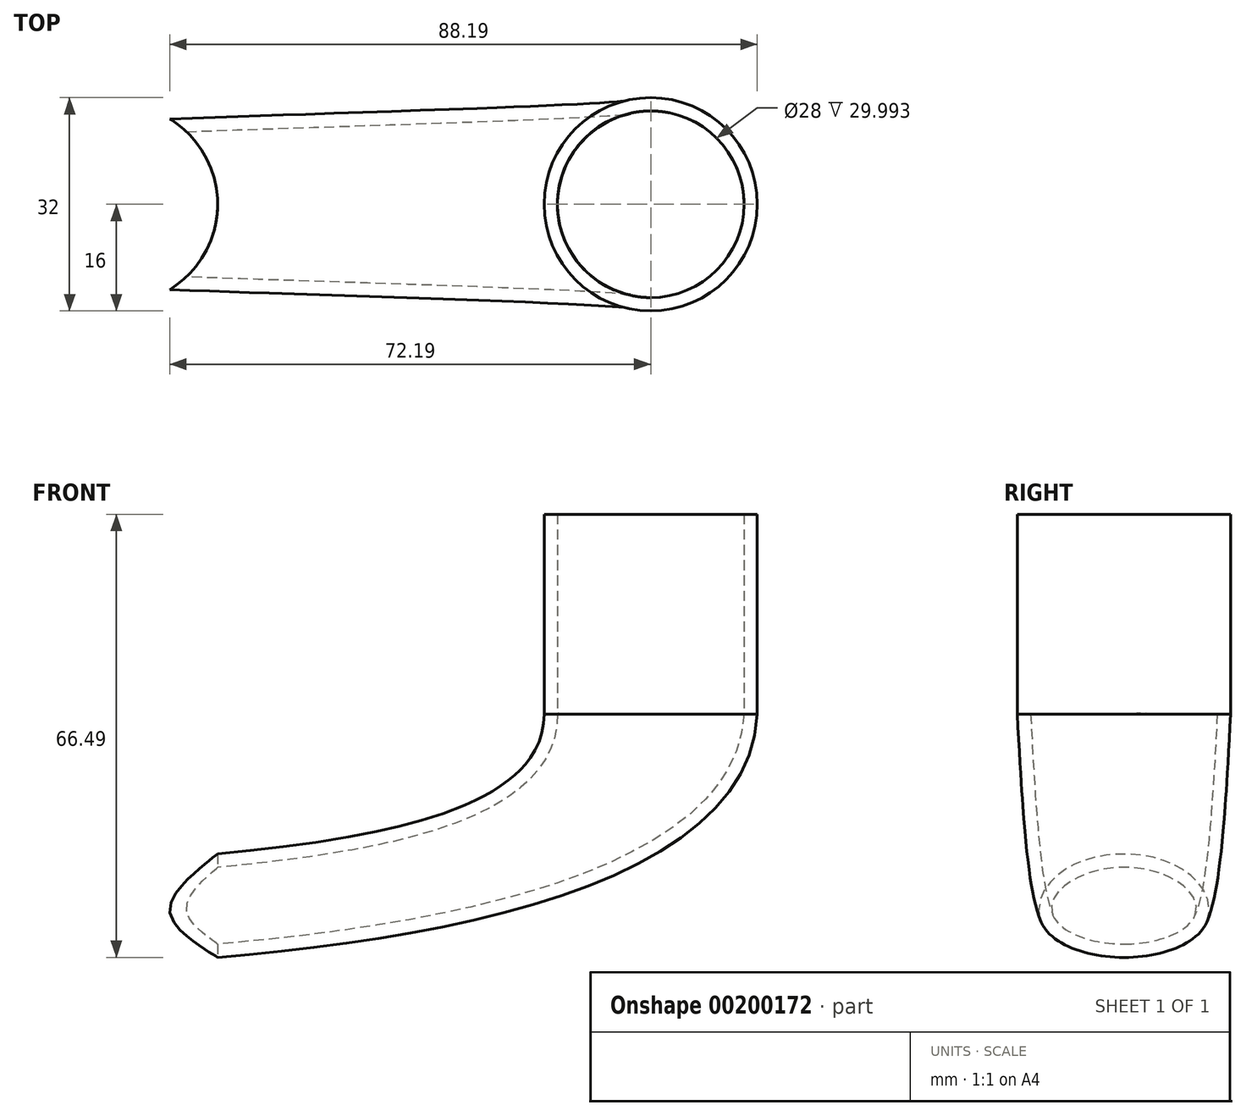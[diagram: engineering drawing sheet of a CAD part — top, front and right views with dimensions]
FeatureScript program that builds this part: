
annotation { "Feature Type Name" : "Feature", "Feature Type Description" : "" }
export const myFeature = defineFeature(function(context is Context, id is Id, definition is map)
    precondition{}
    {
        {
            var Q0;
            Q0=qCreatedBy(makeId("Top.planeOp"),FACE);
            var sketch = newSketch(context, id + "F0", { "sketchPlane" : qUnion([Q0])});
            skLineSegment(sketch, "E0", {"start": v(-83.02, 0) * mm, "end": v(78.58, 0) * mm, "construction": true});
            skArc(sketch, "E1", {"start": v(-16, 0) * mm, "mid": v(0, -16) * mm, "end": v(16, 0) * mm});
            skArc(sketch, "E2", {"start": v(16, 0) * mm, "mid": v(0, 16) * mm, "end": v(-16, 0) * mm});
            skLineSegment(sketch, "E3", {"start": v(0, 24.3) * mm, "end": v(0, 16) * mm, "construction": true});
            skPoint(sketch, "E3.endSnap0", {"position": v(0, -16) * mm});
            skLineSegment(sketch, "E4", {"start": v(0, 16) * mm, "end": v(0, -16) * mm, "construction": true});
            skLineSegment(sketch, "E5", {"start": v(0, -16) * mm, "end": v(0, -22.18) * mm, "construction": true});
            skSolve(sketch);
        }
        {
            var Q0;
            Q0=qCreatedBy(makeId("Right.planeOp"),FACE);
            cPlane(context, id + "F1", {"entities" : qUnion([Q0]), "cplaneType" : CPlaneType.OFFSET, "offset" : 80 * mm, "oppositeDirection" : true, "width" : 150 * mm, "height" : 150 * mm});
        }
        {
            var Q0;
            Q0=qCreatedBy(id+"F1.planeOp",FACE);
            var sketch = newSketch(context, id + "F2", { "sketchPlane" : qUnion([Q0])});
            skEllipticalArc(sketch, "E6", {});
            skEllipticalArc(sketch, "E7", {});
            skEllipticalArc(sketch, "E8", {});
            skEllipticalArc(sketch, "E9", {});
            skLineSegment(sketch, "E10.0", {"start": v(16, 0) * mm, "end": v(-16, 0) * mm, "construction": true});
            const initialGuessF2  = {"E6": [0, -0.03, 1, 0, 0.0125, 0.0075, 3.141592653589793, 4.71238898038469], "E7": [0, -0.03, 1, 0, 0.0125, 0.0075, 0, 1.5707963267948966], "E8": [0, -0.03, 1, 0, 0.0125, 0.0075, 1.5707963267948966, 3.141592653589793], "E9": [0, -0.03, 1, 0, 0.0125, 0.0075, 4.71238898038469, 0]};
            skSetInitialGuess(sketch, initialGuessF2);
            skSolve(sketch);
        }
        {
            var Q0;
            Q0=qCreatedBy(makeId("Front.planeOp"),FACE);
            var sketch = newSketch(context, id + "F3", { "sketchPlane" : qUnion([Q0])});
            skFitSpline(sketch, "E11", {"points": [v(-80, -22.5) * mm, v(-16, 0) * mm], "startDerivative": vector(54.69, 7.04) * mm, "endDerivative": vector(-0.44, 57.87) * mm});
            skFitSpline(sketch, "E12", {"points": [v(-80, -37.5) * mm, v(16, 0) * mm], "startDerivative": vector(113.7, 5.9) * mm, "endDerivative": vector(4.22, 85.94) * mm});
            skSolve(sketch);
        }
        {
            var Q0;
            Q0=makeQuery(id+"F0.imprint","IMPRINT",FACE,{"disambiguationData":[TD([[makeQuery(id+"F0.imprint","IMPRINT",EDGE,{"derivedFrom":sQuery(id+"F0.wireOp",EDGE,"E1")}),1.0]])]});
            var Q1;
            Q1=makeQuery(id+"F2.imprint","IMPRINT",FACE,{"disambiguationData":[TD([[makeQuery(id+"F2.imprint","IMPRINT",EDGE,{"derivedFrom":sQuery(id+"F2.wireOp",EDGE,"E6")}),1.0]])]});
            var Q2;
            Q2=sQuery(id+"F3.wireOp",EDGE,"E12");
            var Q3;
            Q3=sQuery(id+"F3.wireOp",EDGE,"E11");
            loft(context, id + "F4", {"addGuides" : true, "sheetProfilesArray" : [{ "sheetProfileEntities" : qUnion([Q0]) }, { "sheetProfileEntities" : qUnion([Q1]) }], "guidesArray" : [{ "guideEntities" : qUnion([Q2]), "guideDerivativeType" : LoftGuideDerivativeType.DEFAULT, "guideDerivativeMagnitude" : 1 }, { "guideEntities" : qUnion([Q3]), "guideDerivativeType" : LoftGuideDerivativeType.DEFAULT, "guideDerivativeMagnitude" : 1 }]});
        }
        {
            var Q0;
            Q0=makeQuery(id+"F0.imprint","IMPRINT",FACE,{"disambiguationData":[TD([[makeQuery(id+"F0.imprint","IMPRINT",EDGE,{"derivedFrom":sQuery(id+"F0.wireOp",EDGE,"E1")}),1.0]])]});
            extrude(context, id + "F5", {"entities" : qUnion([Q0]), "operationType" : NewBodyOperationType.ADD, "depth" : 30 * mm});
        }
        {
            var Q0;
            Q0=qCreatedBy(makeId("Top.planeOp"),FACE);
            var Q1;
            Q1=sQuery(id+"F2.wireOp",VERTEX,"E6.center");
            cPlane(context, id + "F6", {"entities" : qUnion([Q0, Q1]), "cplaneType" : CPlaneType.PLANE_POINT, "offset" : 25 * mm, "width" : 150 * mm, "height" : 150 * mm});
        }
        {
            var Q0;
            Q0=qCreatedBy(id+"F6.planeOp",FACE);
            var sketch = newSketch(context, id + "F7", { "sketchPlane" : qUnion([Q0])});
            skPoint(sketch, "E13.0", {"position": v(-80, 0) * mm});
            skCircle(sketch, "E14", {"center": v(-80, 0) * mm, "radius": 15 * mm});
            skPoint(sketch, "E15.0", {"position": v(-80, -12.5) * mm});
            skSolve(sketch);
        }
        {
            var Q0;
            Q0=makeQuery(id+"F7.imprint","IMPRINT",FACE,{"disambiguationData":[TD([[makeQuery(id+"F7.imprint","IMPRINT",EDGE,{"derivedFrom":sQuery(id+"F7.wireOp",EDGE,"E14")}),1.0]])]});
            extrude(context, id + "F8", {"entities" : qUnion([Q0]), "endBound" : BoundingType.SYMMETRIC, "depth" : 40 * mm});
        }
        {
            var Q0;
            Q0=makeQuery(id+"F5.opExtrude","CAP_FACE",FACE,{"disambiguationData":[OSD([sQuery(id+"F0.wireOp",EDGE,"E1"),sQuery(id+"F0.wireOp",EDGE,"E2")])],"isStart":false});
            var Q1;
            Q1=makeQuery(id+"F4.opLoft","SWEPT_BODY",BODY,{"disambiguationData":[OSD([makeQuery(id+"F0.imprint","IMPRINT",FACE,{"disambiguationData":[TD([[makeQuery(id+"F0.imprint","IMPRINT",EDGE,{"derivedFrom":sQuery(id+"F0.wireOp",EDGE,"E1")}),1.0]])]}),makeQuery(id+"F2.imprint","IMPRINT",FACE,{"disambiguationData":[TD([[makeQuery(id+"F2.imprint","IMPRINT",EDGE,{"derivedFrom":sQuery(id+"F2.wireOp",EDGE,"E6")}),1.0]])]}),sQuery(id+"F3.wireOp",EDGE,"E11"),sQuery(id+"F3.wireOp",EDGE,"E12")])]});
            shell(context, id + "F9", {"entities" : qUnion([Q0]), "parts" : qUnion([Q1]), "thickness" : 2 * mm});
        }
        {
            var Q0;
            Q0=makeQuery(id+"F8.opExtrude","SWEPT_BODY",BODY,{"disambiguationData":[OSD([sQuery(id+"F7.wireOp",EDGE,"E14")])]});
            var Q1;
            Q1=makeQuery(id+"F4.opLoft","SWEPT_BODY",BODY,{"disambiguationData":[OSD([makeQuery(id+"F0.imprint","IMPRINT",FACE,{"disambiguationData":[TD([[makeQuery(id+"F0.imprint","IMPRINT",EDGE,{"derivedFrom":sQuery(id+"F0.wireOp",EDGE,"E1")}),1.0]])]}),makeQuery(id+"F2.imprint","IMPRINT",FACE,{"disambiguationData":[TD([[makeQuery(id+"F2.imprint","IMPRINT",EDGE,{"derivedFrom":sQuery(id+"F2.wireOp",EDGE,"E6")}),1.0]])]}),sQuery(id+"F3.wireOp",EDGE,"E11"),sQuery(id+"F3.wireOp",EDGE,"E12")])]});
            booleanBodies(context, id + "F10", {"operationType" : BooleanOperationType.SUBTRACTION, "tools" : qUnion([Q0]), "targets" : qUnion([Q1])});
        }
    });
